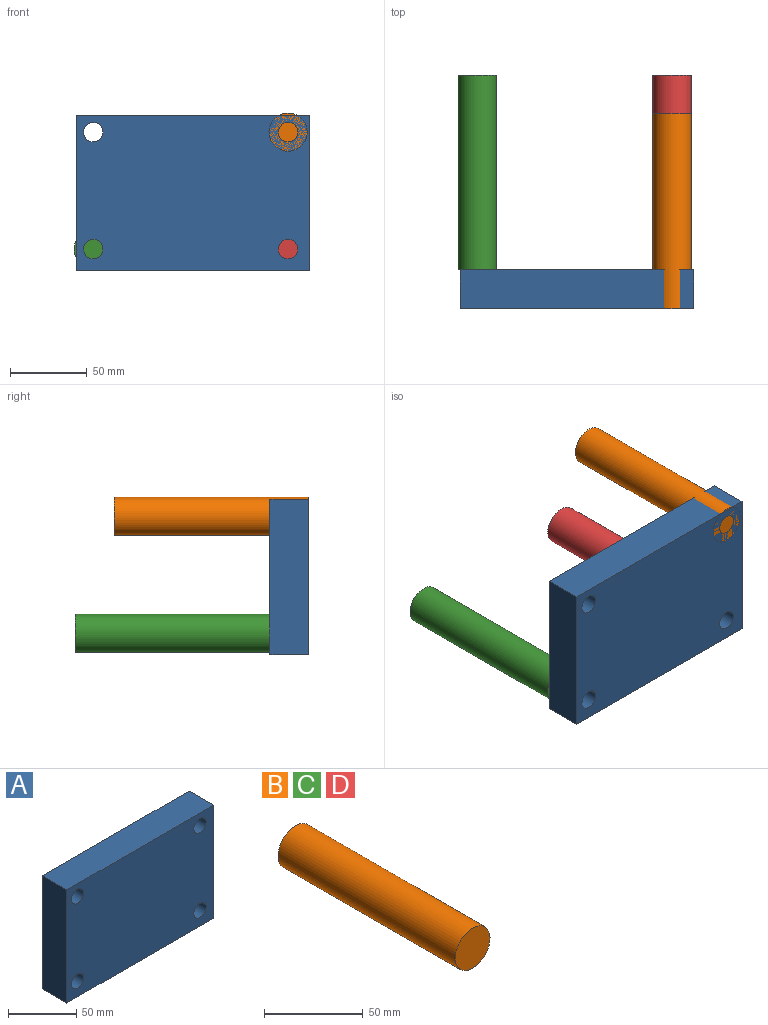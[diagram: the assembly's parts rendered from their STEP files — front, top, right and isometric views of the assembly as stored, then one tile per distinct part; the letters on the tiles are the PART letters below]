
ASSEMBLY  parts=4 mates=3
PART A: 10 faces, bbox 152.4x25.4x101.6 mm
  f0: cylinder r=6.35mm len=25.4mm, axis (0,-1,0), area 1013.4mm2, adj f7,f8
  f1: cylinder r=6.35mm len=25.4mm, axis (0,-1,0), area 1013.4mm2, adj f7,f8
  f2: cylinder r=6.35mm len=25.4mm, axis (0,-1,0), area 1013.4mm2, adj f7,f8
  f3: plane 152.4x25.4mm, normal (0,0,-1), area 3871mm2, adj f4,f6,f7,f8
  f4: plane 101.6x25.4mm, normal (1,0,0), area 2580.6mm2, adj f3,f5,f7,f8
  f5: plane 152.4x25.4mm, normal (0,0,1), area 3871mm2, adj f4,f6,f7,f8
  f6: plane 101.6x25.4mm, normal (-1,0,0), area 2580.6mm2, adj f3,f5,f7,f8
  f7: plane 152.4x101.6mm, normal (0,-1,0), area 14977.1mm2, adj f0,f1,f2,f3,f4,f5,f6,f9
  f8: plane 152.4x101.6mm, normal (0,1,0), area 14977.1mm2, adj f0,f1,f2,f3,f4,f5,f6,f9
  f9: cylinder r=6.35mm len=25.4mm, axis (0,-1,0), area 1013.4mm2, adj f7,f8
PART B: 3 faces, bbox 24.9x127x24.9 mm
  f0: cylinder r=12.45mm len=127mm, axis (0,1,0), area 9931.5mm2, adj f1,f2
  f1: plane 24.89x24.89mm, normal (0,-1,0), area 486.6mm2, adj f0
  f2: plane 24.89x24.89mm, normal (0,1,0), area 486.6mm2, adj f0
PART C: same geometry as B
PART D: same geometry as B
PLACE A t=(-76.18,-75.28,-39.42)mm
PLACE B t=(-14.18,26.32,0.19)mm
PLACE C t=(-141.18,51.72,-76.01)mm
PLACE D t=(-14.18,51.72,-76.01)mm
MATE fastened A.f1 <-> B.f0  axis (0,-1,0) through (-14.18,-100.68,0.19)mm
MATE fastened A.f2 <-> C.f0  axis (0,1,0) through (-141.18,-75.28,-76.01)mm
MATE fastened A.f0 <-> D.f0  axis (0,1,0) through (-14.18,-75.28,-76.01)mm
